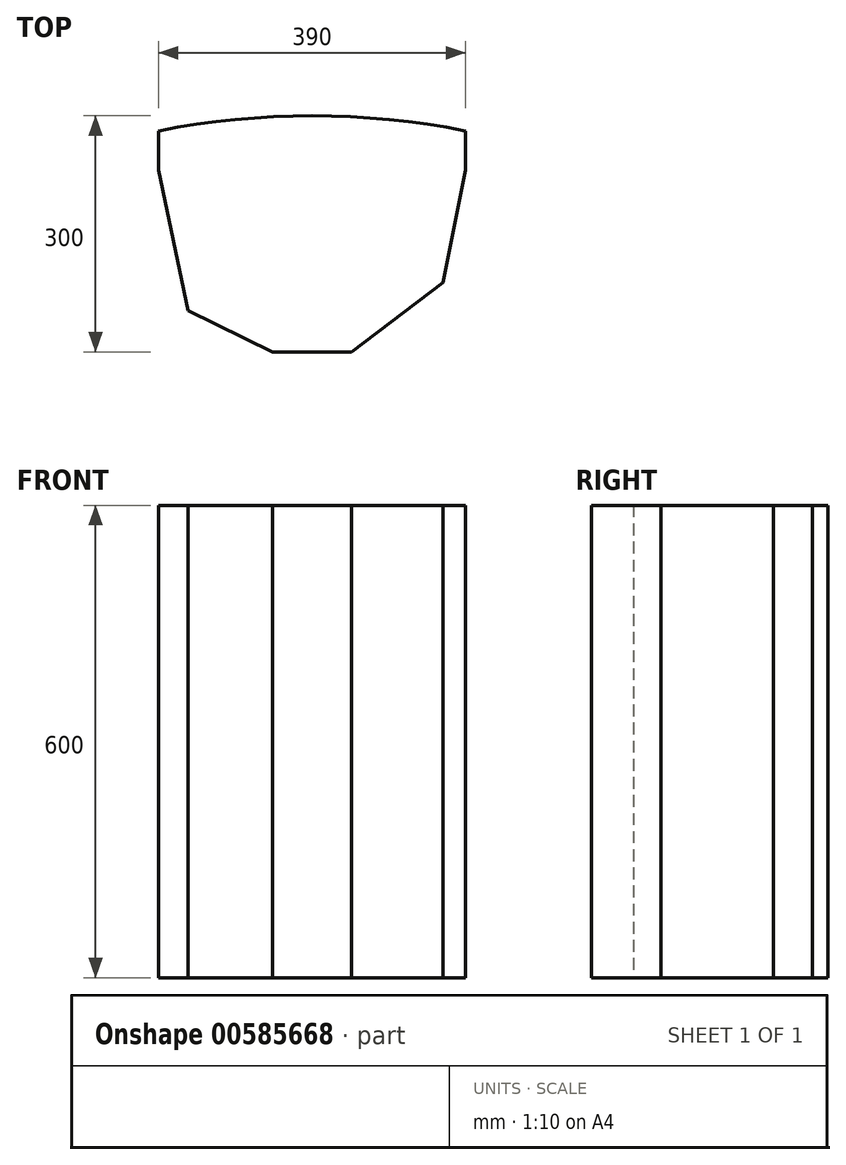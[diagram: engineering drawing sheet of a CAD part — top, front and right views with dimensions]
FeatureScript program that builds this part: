
annotation { "Feature Type Name" : "Feature", "Feature Type Description" : "" }
export const myFeature = defineFeature(function(context is Context, id is Id, definition is map)
    precondition{}
    {
        {
            var Q0;
            Q0=qCreatedBy(makeId("Top.planeOp"),FACE);
            var sketch = newSketch(context, id + "F0", { "sketchPlane" : qUnion([Q0])});
            skArc(sketch, "E0", {"start": v(195, 0) * mm, "mid": v(0, 19.2) * mm, "end": v(-195, 0) * mm});
            skLineSegment(sketch, "E1", {"start": v(-195, 0) * mm, "end": v(-195, -50) * mm});
            skLineSegment(sketch, "E2", {"start": v(-195, -50) * mm, "end": v(-157.8, -227.93) * mm});
            skLineSegment(sketch, "E3", {"start": v(-157.8, -227.93) * mm, "end": v(-50, -280.8) * mm});
            skLineSegment(sketch, "E4", {"start": v(-50, -280.8) * mm, "end": v(50, -280.8) * mm});
            skLineSegment(sketch, "E5", {"start": v(50, -280.8) * mm, "end": v(166.34, -192.94) * mm});
            skLineSegment(sketch, "E6", {"start": v(166.34, -192.94) * mm, "end": v(195, -50) * mm});
            skLineSegment(sketch, "E7", {"start": v(195, -50) * mm, "end": v(195, 0) * mm});
            skPoint(sketch, "E8", {"position": v(0, -280.8) * mm});
            skSolve(sketch);
        }
        {
            var Q0;
            Q0=qSketchRegion(id+"F0",true);
            extrude(context, id + "F1", {"entities" : qUnion([Q0]), "endBound" : BoundingType.SYMMETRIC, "depth" : 600 * mm, "offsetDistance" : 25 * mm});
        }
    });
